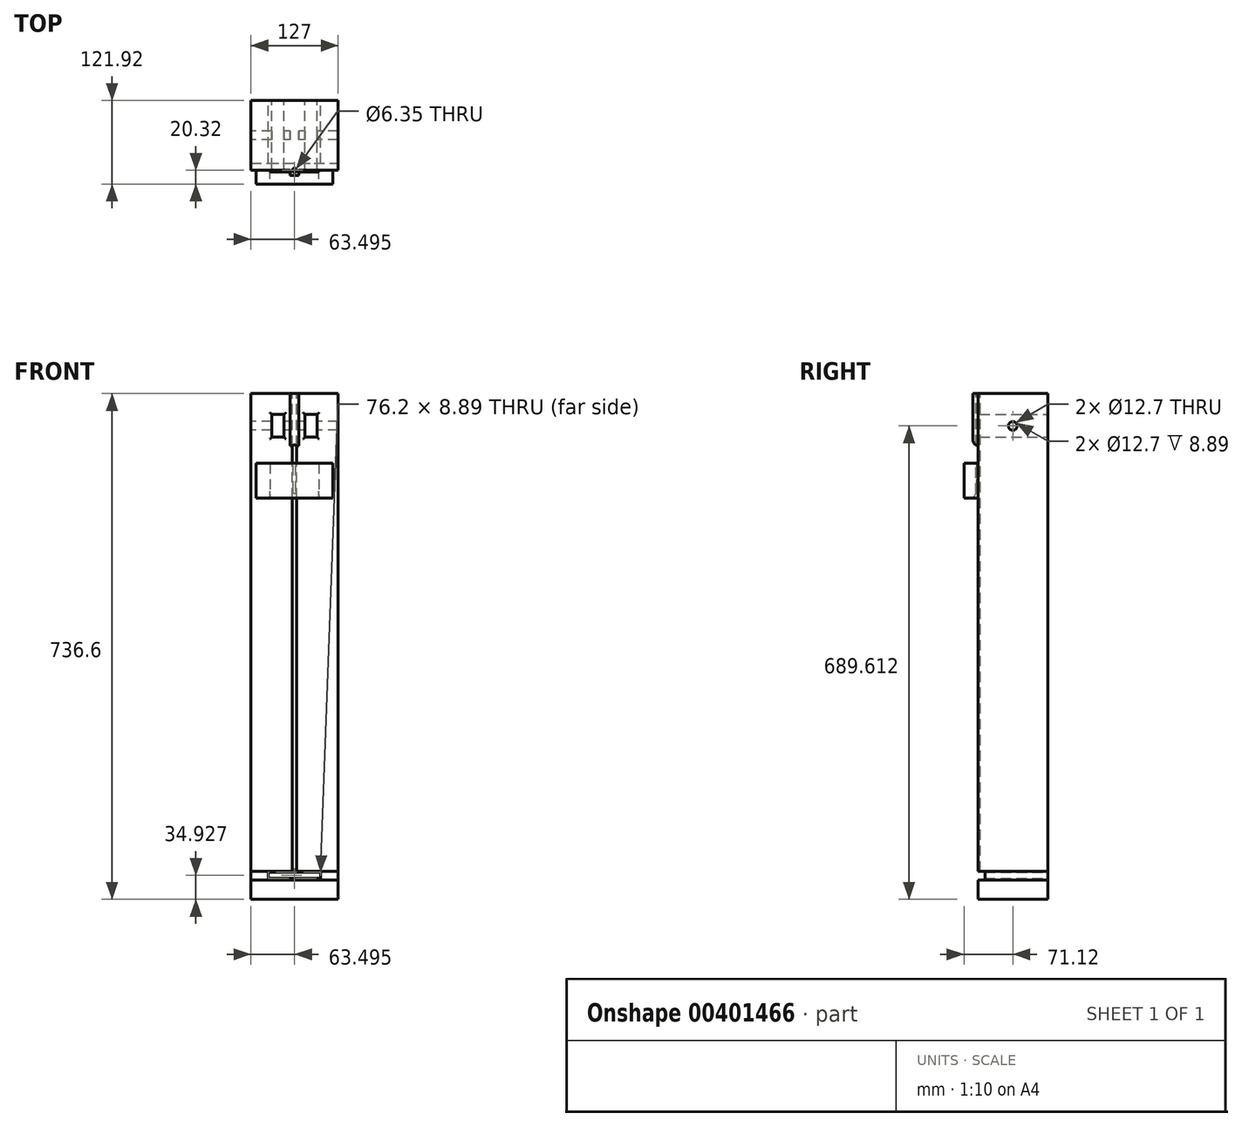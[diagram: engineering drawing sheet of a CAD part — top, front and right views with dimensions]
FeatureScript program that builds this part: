
annotation { "Feature Type Name" : "Feature", "Feature Type Description" : "" }
export const myFeature = defineFeature(function(context is Context, id is Id, definition is map)
    precondition{}
    {
        {
            var Q0;
            Q0=qCreatedBy(makeId("Front.planeOp"),FACE);
            var sketch = newSketch(context, id + "F0", { "sketchPlane" : qUnion([Q0])});
            skLineSegment(sketch, "E0.bottom", {"start": v(-84.3, 653.2) * mm, "end": v(42.7, 653.2) * mm});
            skLineSegment(sketch, "E0.top", {"start": v(-84.3, -83.4) * mm, "end": v(42.7, -83.4) * mm});
            skLineSegment(sketch, "E0.left", {"start": v(-84.3, 653.2) * mm, "end": v(-84.3, -83.4) * mm});
            skLineSegment(sketch, "E0.right", {"start": v(42.7, 653.2) * mm, "end": v(42.7, -83.4) * mm});
            skPoint(sketch, "E1.startSnap0", {"position": v(-20.8, 653.2) * mm});
            skPoint(sketch, "E2.orphan", {"position": v(-20.8, -83.4) * mm});
            skPoint(sketch, "E3.orphan", {"position": v(-84.3, -75.34) * mm});
            skPoint(sketch, "E4.orphan", {"position": v(42.7, -75.34) * mm});
            skLineSegment(sketch, "E5.bottom", {"start": v(12.23, 589.7) * mm, "end": v(-5.55, 589.7) * mm});
            skLineSegment(sketch, "E5.top", {"start": v(12.23, 622.71) * mm, "end": v(-5.55, 622.71) * mm});
            skLineSegment(sketch, "E5.left", {"start": v(12.23, 589.7) * mm, "end": v(12.23, 622.71) * mm});
            skLineSegment(sketch, "E5.right", {"start": v(-5.55, 589.7) * mm, "end": v(-5.55, 622.71) * mm});
            skLineSegment(sketch, "E6.bottom", {"start": v(-36.03, 589.7) * mm, "end": v(-53.81, 589.7) * mm});
            skLineSegment(sketch, "E6.top", {"start": v(-36.03, 622.71) * mm, "end": v(-53.81, 622.71) * mm});
            skLineSegment(sketch, "E6.left", {"start": v(-36.03, 589.7) * mm, "end": v(-36.03, 622.71) * mm});
            skLineSegment(sketch, "E6.right", {"start": v(-53.81, 589.7) * mm, "end": v(-53.81, 622.71) * mm});
            skLineSegment(sketch, "E7.bottom", {"start": v(-58.9, -52.93) * mm, "end": v(17.3, -52.93) * mm});
            skLineSegment(sketch, "E7.top", {"start": v(-58.9, -44.04) * mm, "end": v(17.3, -44.04) * mm});
            skLineSegment(sketch, "E7.left", {"start": v(-58.9, -52.93) * mm, "end": v(-58.9, -44.04) * mm});
            skLineSegment(sketch, "E7.right", {"start": v(17.3, -52.93) * mm, "end": v(17.3, -44.04) * mm});
            skLineSegment(sketch, "E8", {"start": v(-84.3, -42.77) * mm, "end": v(42.7, -42.77) * mm});
            skLineSegment(sketch, "E9", {"start": v(-84.3, -55.47) * mm, "end": v(42.7, -55.47) * mm});
            skLineSegment(sketch, "E10", {"start": v(42.7, 577) * mm, "end": v(-84.3, 577) * mm});
            skLineSegment(sketch, "E11", {"start": v(-14.44, 577) * mm, "end": v(-14.44, 653.2) * mm});
            skLineSegment(sketch, "E12", {"start": v(-27.14, 577) * mm, "end": v(-27.14, 653.2) * mm});
            skLineSegment(sketch, "E13.bottom", {"start": v(35.09, 551.6) * mm, "end": v(14.77, 551.6) * mm});
            skLineSegment(sketch, "E13.top", {"start": v(35.09, 500.8) * mm, "end": v(14.77, 500.8) * mm});
            skLineSegment(sketch, "E13.left", {"start": v(35.09, 551.6) * mm, "end": v(35.09, 500.8) * mm});
            skLineSegment(sketch, "E13.right", {"start": v(14.77, 551.6) * mm, "end": v(14.77, 500.8) * mm});
            skLineSegment(sketch, "E14.bottom", {"start": v(-56.35, 551.6) * mm, "end": v(-76.67, 551.6) * mm});
            skLineSegment(sketch, "E14.top", {"start": v(-56.35, 500.8) * mm, "end": v(-76.67, 500.8) * mm});
            skLineSegment(sketch, "E14.left", {"start": v(-56.35, 551.6) * mm, "end": v(-56.35, 500.8) * mm});
            skLineSegment(sketch, "E14.right", {"start": v(-76.67, 551.6) * mm, "end": v(-76.67, 500.8) * mm});
            skSolve(sketch);
        }
        {
            var Q0;
            {var subQ0=sQuery(id+"F0.wireOp",EDGE,"Peh61ck8-LRfF-V716-9MEI-FhPaOjtmJK3p");var subQ5=sQuery(id+"F0.wireOp",EDGE,"hPy49TnG-zmtl-kgSC-38cS-03U7uKBepyen");var subQ6=makeQuery(id+"F0.imprint","INTERSECT",VERTEX,{"derivedFrom":[subQ5,subQ0]});Q0=makeQuery(id+"F0.imprint","IMPRINT",FACE,{"disambiguationData":[TD([[makeQuery(id+"F0.imprint","IMPRINT",EDGE,{"disambiguationData":[TD([[subQ6,1.0]])],"derivedFrom":subQ5}),1.0]])]});}
            var Q1;
            {var subQ0=sQuery(id+"F0.wireOp",EDGE,"YcieJJtT-WS2f-e4Z8-cfPE-g1vHEIGdeXCo");var subQ5=sQuery(id+"F0.wireOp",EDGE,"hPy49TnG-zmtl-kgSC-38cS-03U7uKBepyen");var subQ6=makeQuery(id+"F0.imprint","INTERSECT",VERTEX,{"derivedFrom":[subQ5,subQ0]});Q1=makeQuery(id+"F0.imprint","IMPRINT",FACE,{"disambiguationData":[TD([[makeQuery(id+"F0.imprint","IMPRINT",EDGE,{"disambiguationData":[TD([[subQ6,-1.0]])],"derivedFrom":subQ5}),1.0]])]});}
            var Q2;
            {var subQ0=sQuery(id+"F0.wireOp",EDGE,"E0.top");Q2=makeQuery(id+"F0.imprint","IMPRINT",FACE,{"disambiguationData":[TD([[makeQuery(id+"F0.imprint","IMPRINT",EDGE,{"derivedFrom":subQ0}),1.0]])]});}
            var Q3;
            {var subQ0=sQuery(id+"F0.wireOp",EDGE,"E8");Q3=makeQuery(id+"F0.imprint","IMPRINT",FACE,{"disambiguationData":[TD([[makeQuery(id+"F0.imprint","IMPRINT",EDGE,{"derivedFrom":subQ0}),1.0]])]});}
            var Q4;
            Q4=makeQuery(id+"F0.imprint","IMPRINT",FACE,{"disambiguationData":[TD([[makeQuery(id+"F0.imprint","IMPRINT",EDGE,{"derivedFrom":sQuery(id+"F0.wireOp",EDGE,"E5.bottom")}),1.0]])]});
            var Q5;
            Q5=makeQuery(id+"F0.imprint","IMPRINT",FACE,{"disambiguationData":[TD([[makeQuery(id+"F0.imprint","IMPRINT",EDGE,{"derivedFrom":sQuery(id+"F0.wireOp",EDGE,"E6.bottom")}),1.0]])]});
            extrude(context, id + "F1", {"entities" : qUnion([Q0, Q1, Q2, Q3, Q4, Q5]), "depth" : 101.6 * mm});
        }
        {
            var Q0;
            Q0=makeQuery(id+"F1.opExtrude","SWEPT_FACE",FACE,{"disambiguationData":[OSD([sQuery(id+"F0.wireOp",EDGE,"E0.bottom")])]});
            var sketch = newSketch(context, id + "F2", { "sketchPlane" : qUnion([Q0])});
            skPoint(sketch, "E15", {"position": v(-20.8, -101.6) * mm});
            skPoint(sketch, "E16", {"position": v(-84.3, -101.6) * mm});
            skPoint(sketch, "E17", {"position": v(42.7, -101.6) * mm});
            skSolve(sketch);
        }
        {
            var Q0;
            Q0=makeQuery(id+"F1.opExtrude","CAP_EDGE",EDGE,{"disambiguationData":[OSD([sQuery(id+"F0.wireOp",EDGE,"E5.left")])],"isStart":false});
            var Q1;
            Q1=makeQuery(id+"F1.opExtrude","CAP_EDGE",EDGE,{"disambiguationData":[OSD([sQuery(id+"F0.wireOp",EDGE,"E5.bottom")])],"isStart":false});
            var Q2;
            Q2=makeQuery(id+"F1.opExtrude","CAP_EDGE",EDGE,{"disambiguationData":[OSD([sQuery(id+"F0.wireOp",EDGE,"E5.right")])],"isStart":false});
            var Q3;
            Q3=makeQuery(id+"F1.opExtrude","CAP_EDGE",EDGE,{"disambiguationData":[OSD([sQuery(id+"F0.wireOp",EDGE,"E5.top")])],"isStart":false});
            var Q4;
            Q4=makeQuery(id+"F1.opExtrude","CAP_EDGE",EDGE,{"disambiguationData":[OSD([sQuery(id+"F0.wireOp",EDGE,"E6.left")])],"isStart":false});
            var Q5;
            Q5=makeQuery(id+"F1.opExtrude","CAP_EDGE",EDGE,{"disambiguationData":[OSD([sQuery(id+"F0.wireOp",EDGE,"E6.top")])],"isStart":false});
            var Q6;
            Q6=makeQuery(id+"F1.opExtrude","CAP_EDGE",EDGE,{"disambiguationData":[OSD([sQuery(id+"F0.wireOp",EDGE,"E6.right")])],"isStart":false});
            var Q7;
            Q7=makeQuery(id+"F1.opExtrude","CAP_EDGE",EDGE,{"disambiguationData":[OSD([sQuery(id+"F0.wireOp",EDGE,"E6.bottom")])],"isStart":false});
            fillet(context, id + "F3", {"entities" : qUnion([Q0, Q1, Q2, Q3, Q4, Q5, Q6, Q7]), "radius" : 2.54 * mm, "tangentPropagation" : true, "allowEdgeOverflow" : false});
        }
        {
            var Q0;
            Q0=makeQuery(id+"F0.imprint","IMPRINT",FACE,{"disambiguationData":[TD([[makeQuery(id+"F0.imprint","IMPRINT",EDGE,{"derivedFrom":sQuery(id+"F0.wireOp",EDGE,"E7.bottom")}),-1.0]])]});
            extrude(context, id + "F4", {"entities" : qUnion([Q0]), "depth" : 91.44 * mm});
        }
        {
            var Q0;
            {var subQ0=sQuery(id+"F0.wireOp",EDGE,"E0.left");Q0=makeQuery(id+"F1.opExtrude","SWEPT_FACE",FACE,{"disambiguationData":[OSD([subQ0]),TDD([makeQuery(id+"F0.imprint","IMPRINT",EDGE,{"disambiguationData":[TD([[makeQuery(id+"F0.imprint","INTERSECT",VERTEX,{"derivedFrom":[sQuery(id+"F0.wireOp",EDGE,"E0.bottom"),subQ0]}),-1.0]])],"derivedFrom":subQ0})])]});}
            var sketch = newSketch(context, id + "F5", { "sketchPlane" : qUnion([Q0])});
            skPoint(sketch, "E18", {"position": v(101.6, 653.2) * mm});
            skLineSegment(sketch, "E19.bottom", {"start": v(101.6, 653.2) * mm, "end": v(50.8, 653.2) * mm});
            skLineSegment(sketch, "E19.top", {"start": v(101.6, 606.2) * mm, "end": v(50.8, 606.2) * mm});
            skLineSegment(sketch, "E19.left", {"start": v(101.6, 653.2) * mm, "end": v(101.6, 606.2) * mm});
            skLineSegment(sketch, "E19.right", {"start": v(50.8, 653.2) * mm, "end": v(50.8, 606.2) * mm});
            skPoint(sketch, "E20", {"position": v(50.8, 606.2) * mm});
            skSolve(sketch);
        }
        {
            var Q0;
            Q0=sQuery(id+"F5.wireOp",VERTEX,"E20");
            var Q1;
            Q1=makeQuery(id+"F1.opExtrude","SWEPT_BODY",BODY,{"disambiguationData":[OSD([sQuery(id+"F0.wireOp",EDGE,"E0.bottom"),sQuery(id+"F0.wireOp",EDGE,"E0.left"),sQuery(id+"F0.wireOp",EDGE,"E0.right"),sQuery(id+"F0.wireOp",EDGE,"E5.bottom"),sQuery(id+"F0.wireOp",EDGE,"E5.top"),sQuery(id+"F0.wireOp",EDGE,"E5.left"),sQuery(id+"F0.wireOp",EDGE,"E5.right"),sQuery(id+"F0.wireOp",EDGE,"E6.bottom"),sQuery(id+"F0.wireOp",EDGE,"E6.top"),sQuery(id+"F0.wireOp",EDGE,"E6.left"),sQuery(id+"F0.wireOp",EDGE,"E6.right"),sQuery(id+"F0.wireOp",EDGE,"E8")])]});
            hole(context, id + "F6", {"style" : HoleStyle.SIMPLE, "endStyle" : HoleEndStyle.BLIND, "holeDiameter" : 12.7 * mm, "holeDepth" : 693.42 * mm, "isTappedThrough" : true, "tappedDepth" : 12.7 * mm, "tapClearance" : 3, "locations" : qUnion([Q0]), "scope" : qUnion([Q1])});
        }
        {
            var Q0;
            {var subQ0=sQuery(id+"F0.wireOp",EDGE,"E11");Q0=makeQuery(id+"F0.imprint","IMPRINT",FACE,{"disambiguationData":[TD([[makeQuery(id+"F0.imprint","IMPRINT",EDGE,{"derivedFrom":subQ0}),1.0]])]});}
            extrude(context, id + "F7", {"entities" : qUnion([Q0]), "operationType" : NewBodyOperationType.ADD, "depth" : 109.22 * mm});
        }
        {
            var Q0;
            Q0=makeQuery(id+"F7.opExtrude","CAP_EDGE",EDGE,{"disambiguationData":[OSD([sQuery(id+"F0.wireOp",EDGE,"E10")])],"isStart":false});
            fillet(context, id + "F8", {"entities" : qUnion([Q0]), "radius" : 10.16 * mm, "tangentPropagation" : true, "allowEdgeOverflow" : false});
        }
        {
            var Q0;
            Q0=makeQuery(id+"F0.imprint","IMPRINT",FACE,{"disambiguationData":[TD([[makeQuery(id+"F0.imprint","IMPRINT",EDGE,{"derivedFrom":sQuery(id+"F0.wireOp",EDGE,"E13.bottom")}),1.0]])]});
            var Q1;
            Q1=makeQuery(id+"F0.imprint","IMPRINT",FACE,{"disambiguationData":[TD([[makeQuery(id+"F0.imprint","IMPRINT",EDGE,{"derivedFrom":sQuery(id+"F0.wireOp",EDGE,"E14.bottom")}),1.0]])]});
            extrude(context, id + "F9", {"entities" : qUnion([Q0, Q1]), "operationType" : NewBodyOperationType.ADD, "depth" : 121.92 * mm});
        }
        {
            var Q0;
            Q0=makeQuery(id+"F9.opExtrude","SWEPT_FACE",FACE,{"disambiguationData":[OSD([sQuery(id+"F0.wireOp",EDGE,"E13.right")])]});
            var sketch = newSketch(context, id + "F10", { "sketchPlane" : qUnion([Q0])});
            skPoint(sketch, "E21", {"position": v(121.92, 551.6) * mm});
            skPoint(sketch, "E22", {"position": v(104.14, 551.6) * mm});
            skPoint(sketch, "E23", {"position": v(121.92, 500.8) * mm});
            skPoint(sketch, "E24", {"position": v(104.14, 500.8) * mm});
            skLineSegment(sketch, "E25", {"start": v(104.14, 551.6) * mm, "end": v(104.14, 500.8) * mm});
            skSolve(sketch);
        }
        {
            var Q0;
            {var subQ0=sQuery(id+"F10.wireOp",EDGE,"E25");Q0=makeQuery(id+"F10.imprint","IMPRINT",FACE,{"disambiguationData":[TD([[makeQuery(id+"F10.imprint","IMPRINT",EDGE,{"derivedFrom":subQ0}),1.0]])]});}
            extrude(context, id + "F11", {"entities" : qUnion([Q0]), "operationType" : NewBodyOperationType.ADD, "depth" : 71.12 * mm});
        }
        {
            var Q0;
            Q0=sQuery(id+"F2.wireOp",VERTEX,"E15");
            var Q1;
            Q1=makeQuery(id+"F1.opExtrude","SWEPT_BODY",BODY,{"disambiguationData":[OSD([sQuery(id+"F0.wireOp",EDGE,"E0.bottom"),sQuery(id+"F0.wireOp",EDGE,"E0.left"),sQuery(id+"F0.wireOp",EDGE,"E0.right"),sQuery(id+"F0.wireOp",EDGE,"E5.bottom"),sQuery(id+"F0.wireOp",EDGE,"E5.top"),sQuery(id+"F0.wireOp",EDGE,"E5.left"),sQuery(id+"F0.wireOp",EDGE,"E5.right"),sQuery(id+"F0.wireOp",EDGE,"E6.bottom"),sQuery(id+"F0.wireOp",EDGE,"E6.top"),sQuery(id+"F0.wireOp",EDGE,"E6.left"),sQuery(id+"F0.wireOp",EDGE,"E6.right"),sQuery(id+"F0.wireOp",EDGE,"E8"),sQuery(id+"F0.wireOp",EDGE,"E10"),sQuery(id+"F0.wireOp",EDGE,"E11"),sQuery(id+"F0.wireOp",EDGE,"E12"),sQuery(id+"F0.wireOp",EDGE,"E13.bottom"),sQuery(id+"F0.wireOp",EDGE,"E13.top"),sQuery(id+"F0.wireOp",EDGE,"E13.left"),sQuery(id+"F0.wireOp",EDGE,"E13.right"),sQuery(id+"F0.wireOp",EDGE,"E14.bottom"),sQuery(id+"F0.wireOp",EDGE,"E14.top"),sQuery(id+"F0.wireOp",EDGE,"E14.left"),sQuery(id+"F0.wireOp",EDGE,"E14.right")])]});
            hole(context, id + "F12", {"style" : HoleStyle.SIMPLE, "endStyle" : HoleEndStyle.BLIND, "holeDiameter" : 6.35 * mm, "holeDepth" : 701.04 * mm, "isTappedThrough" : true, "tappedDepth" : 12.7 * mm, "tapClearance" : 3, "locations" : qUnion([Q0]), "scope" : qUnion([Q1])});
        }
        {
            var Q0;
            {var subQ0=sQuery(id+"F10.wireOp",EDGE,"E25");var subQ1=sQuery(id+"F0.wireOp",EDGE,"E13.right");var subQ2=sQuery(id+"F0.wireOp",EDGE,"E13.top");Q0=makeQuery(id+"F12.hole-0.boolean.opBoolean","SPLIT",EDGE,{"disambiguationData":[TD([makeQuery(id+"F9.opExtrude","SWEPT_FACE",FACE,{"disambiguationData":[OSD([subQ1])]})])],"derivedFrom":makeQuery(id+"F11.opExtrude","SWEPT_EDGE",EDGE,{"disambiguationData":[OSD([subQ2,subQ1,subQ0])]})});}
            var Q1;
            {var subQ0=sQuery(id+"F0.wireOp",EDGE,"E13.right");var subQ1=sQuery(id+"F0.wireOp",EDGE,"E13.top");var subQ2=sQuery(id+"F10.wireOp",EDGE,"E25");Q1=makeQuery(id+"F12.hole-0.boolean.opBoolean","SPLIT",EDGE,{"disambiguationData":[TD([makeQuery(id+"F9.opExtrude","SWEPT_FACE",FACE,{"disambiguationData":[OSD([sQuery(id+"F0.wireOp",EDGE,"E14.left")])]})])],"derivedFrom":makeQuery(id+"F11.opExtrude","SWEPT_EDGE",EDGE,{"disambiguationData":[OSD([subQ1,subQ0,subQ2])]})});}
            fillet(context, id + "F13", {"entities" : qUnion([Q0, Q1]), "radius" : 10.16 * mm, "tangentPropagation" : true, "allowEdgeOverflow" : false});
        }
    });
